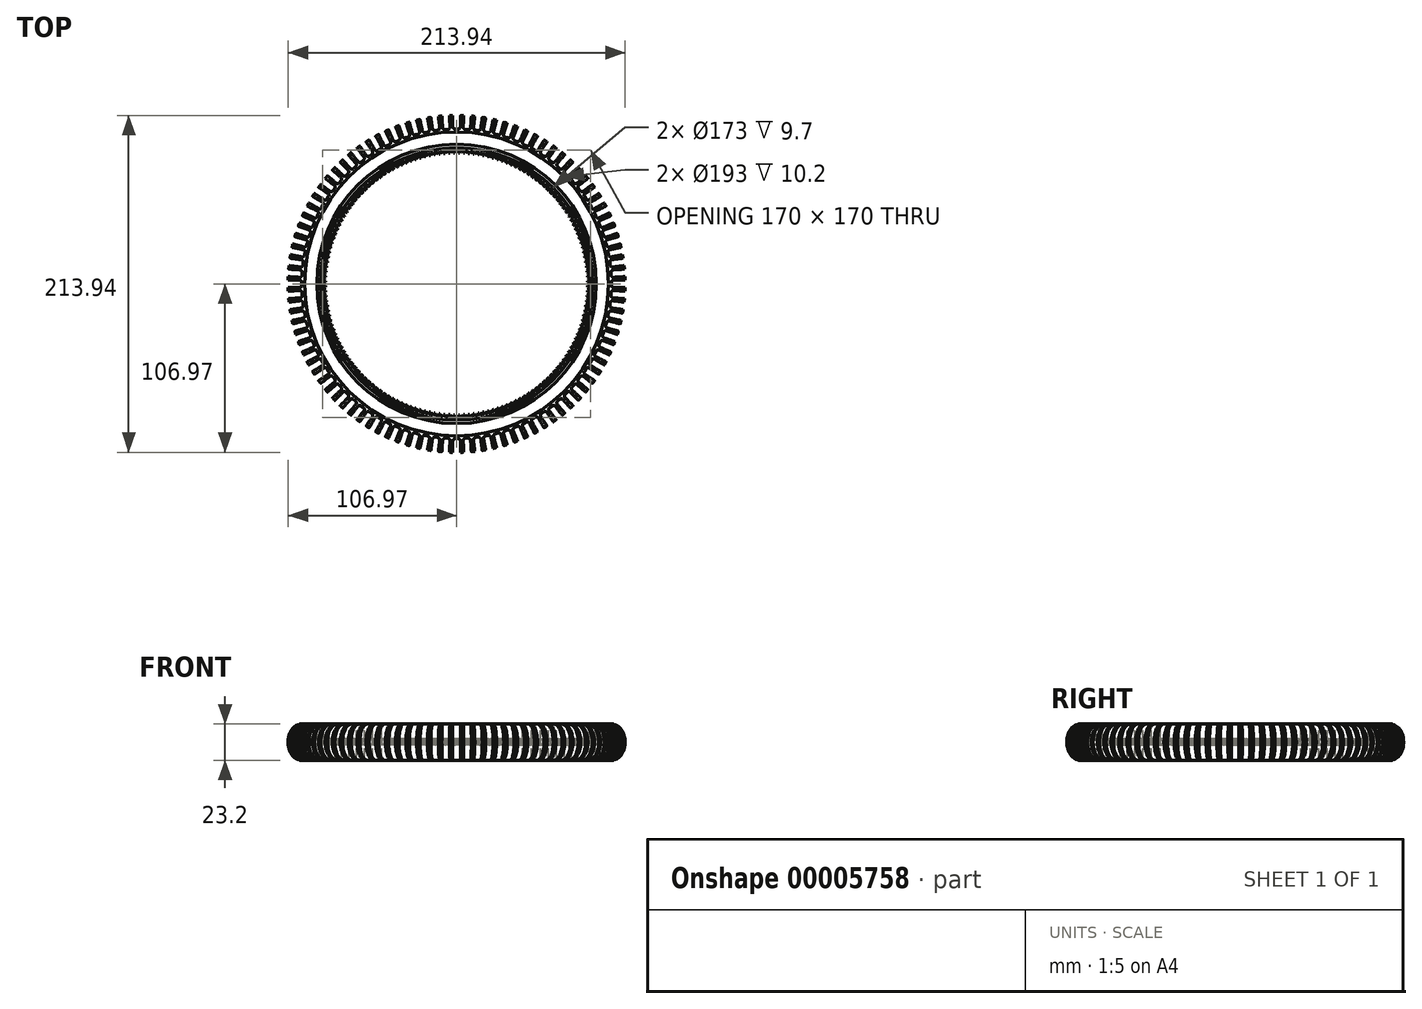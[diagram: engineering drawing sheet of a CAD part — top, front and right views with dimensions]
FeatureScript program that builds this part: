
annotation { "Feature Type Name" : "Feature", "Feature Type Description" : "" }
export const myFeature = defineFeature(function(context is Context, id is Id, definition is map)
    precondition{}
    {
        {
            var Q0;
            Q0=qCreatedBy(makeId("Top.planeOp"),FACE);
            var sketch = newSketch(context, id + "F0", { "sketchPlane" : qUnion([Q0])});
            skCircle(sketch, "E0", {"center": v(0, 0) * mm, "radius": 108 * mm, "construction": true});
            skCircle(sketch, "E1", {"center": v(0, 0) * mm, "radius": 107 * mm});
            skCircle(sketch, "E2", {"center": v(0, 0) * mm, "radius": 86.5 * mm});
            skSolve(sketch);
        }
        {
            var Q0;
            Q0=qCreatedBy(makeId("Top.planeOp"),FACE);
            var sketch = newSketch(context, id + "F1", { "sketchPlane" : qUnion([Q0])});
            skCircle(sketch, "E3", {"center": v(0, 0) * mm, "radius": 88.7 * mm});
            skCircle(sketch, "E4", {"center": v(0, 0) * mm, "radius": 96.5 * mm});
            skCircle(sketch, "E5", {"center": v(0, 0) * mm, "radius": 98.3 * mm});
            skSolve(sketch);
        }
        {
            var Q0;
            Q0=qCreatedBy(makeId("Front.planeOp"),FACE);
            var sketch = newSketch(context, id + "F2", { "sketchPlane" : qUnion([Q0])});
            skLineSegment(sketch, "E6", {"start": v(96.5, 11.6) * mm, "end": v(96.5, 1.4) * mm});
            skLineSegment(sketch, "E7", {"start": v(96.5, 1.4) * mm, "end": v(88.7, 1.4) * mm});
            skLineSegment(sketch, "E8", {"start": v(88.7, 1.4) * mm, "end": v(88.7, 11.6) * mm});
            skLineSegment(sketch, "E9", {"start": v(88.7, 11.6) * mm, "end": v(86.5, 11.6) * mm});
            skLineSegment(sketch, "E10", {"start": v(86.5, 11.6) * mm, "end": v(86.5, -11.6) * mm});
            skLineSegment(sketch, "E11", {"start": v(86.5, 0) * mm, "end": v(0, 0) * mm, "construction": true});
            skLineSegment(sketch, "E12", {"start": v(96.5, 11.6) * mm, "end": v(98.3, 11.6) * mm});
            skLineSegment(sketch, "E13", {"start": v(98.3, 11.6) * mm, "end": v(98.3, 0) * mm, "construction": true});
            skLineSegment(sketch, "E14", {"start": v(88.7, 11.6) * mm, "end": v(96.5, 11.6) * mm, "construction": true});
            skLineSegment(sketch, "E15", {"start": v(88.7, 1.4) * mm, "end": v(88.7, 0) * mm, "construction": true});
            skLineSegment(sketch, "E16", {"start": v(96.5, 1.4) * mm, "end": v(96.5, 0) * mm, "construction": true});
            skLineSegment(sketch, "E17.0.MirrorCS", {"start": v(88.7, -11.6) * mm, "end": v(86.5, -11.6) * mm});
            skLineSegment(sketch, "E18.0.MirrorCS", {"start": v(88.7, -1.4) * mm, "end": v(88.7, -11.6) * mm});
            skLineSegment(sketch, "E19.0.MirrorCS", {"start": v(96.5, -1.4) * mm, "end": v(88.7, -1.4) * mm});
            skLineSegment(sketch, "E20.0.MirrorCS", {"start": v(96.5, -11.6) * mm, "end": v(96.5, -1.4) * mm});
            skLineSegment(sketch, "E21.0.MirrorCS", {"start": v(96.5, -11.6) * mm, "end": v(98.3, -11.6) * mm});
            skEllipticalArc(sketch, "E22", {});
            skLineSegment(sketch, "E23", {"start": v(98.3, 0) * mm, "end": v(107, 0) * mm, "construction": true});
            skLineSegment(sketch, "E24", {"start": v(0, 11.6) * mm, "end": v(0, -11.6) * mm, "construction": true});
            const initialGuessF2  = {"E22": [0.0983, 0, 0, 1, 0.0116, 0.0087, 3.141592653589793, 0]};
            skSetInitialGuess(sketch, initialGuessF2);
            skSolve(sketch);
        }
        {
            var Q0;
            Q0=makeQuery(id+"F2.imprint","IMPRINT",FACE,{"disambiguationData":[TD([[makeQuery(id+"F2.imprint","IMPRINT",EDGE,{"derivedFrom":sQuery(id+"F2.wireOp",EDGE,"E6")}),1.0]])]});
            var Q1;
            Q1=sQuery(id+"F2.wireOp",EDGE,"E24");
            revolve(context, id + "F3", {"entities" : qUnion([Q0]), "axis" : qUnion([Q1]), "revolveType" : RevolveType.FULL});
        }
        {
            var Q0;
            Q0=qCreatedBy(makeId("Top.planeOp"),FACE);
            var sketch = newSketch(context, id + "F4", { "sketchPlane" : qUnion([Q0])});
            skLineSegment(sketch, "E25", {"start": v(0, 0) * mm, "end": v(99.8, 2.4) * mm, "construction": true});
            skLineSegment(sketch, "E26", {"start": v(99.8, -2.4) * mm, "end": v(0, 0) * mm, "construction": true});
            skLineSegment(sketch, "E27", {"start": v(99.8, 2.4) * mm, "end": v(108, 2.4) * mm});
            skLineSegment(sketch, "E28", {"start": v(108, 2.4) * mm, "end": v(108, -2.4) * mm});
            skLineSegment(sketch, "E29", {"start": v(108, -2.4) * mm, "end": v(99.8, -2.4) * mm});
            skLineSegment(sketch, "E30", {"start": v(108, 0) * mm, "end": v(0, 0) * mm, "construction": true});
            skArc(sketch, "E31", {"start": v(99.8, 2.4) * mm, "mid": v(98.74, 1.96) * mm, "end": v(98.3, 0.9) * mm});
            skArc(sketch, "E32", {"start": v(99.8, -2.4) * mm, "mid": v(98.74, -1.96) * mm, "end": v(98.3, -0.9) * mm});
            skLineSegment(sketch, "E33", {"start": v(98.3, 0.9) * mm, "end": v(98.3, -0.9) * mm});
            skSolve(sketch);
        }
        {
            var Q0;
            Q0=makeQuery(id+"F4.imprint","IMPRINT",FACE,{"disambiguationData":[TD([[makeQuery(id+"F4.imprint","IMPRINT",EDGE,{"derivedFrom":sQuery(id+"F4.wireOp",EDGE,"E27")}),-1.0]])]});
            extrude(context, id + "F5", {"entities" : qUnion([Q0]), "operationType" : NewBodyOperationType.REMOVE, "oppositeDirection" : true, "depth" : 25 * mm, "symmetric" : true});
        }
        {
            var Q0;
            Q0=makeQuery(id+"F5.boolean.opBoolean","COPY",FACE,{"derivedFrom":makeQuery(id+"F5.opExtrude","SWEPT_FACE",FACE,{"disambiguationData":[OSD([sQuery(id+"F4.wireOp",EDGE,"E27")])]})});
            var Q1;
            Q1=makeQuery(id+"F5.boolean.opBoolean","COPY",FACE,{"derivedFrom":makeQuery(id+"F5.opExtrude","SWEPT_FACE",FACE,{"disambiguationData":[OSD([sQuery(id+"F4.wireOp",EDGE,"E31")])]})});
            var Q2;
            Q2=makeQuery(id+"F5.boolean.opBoolean","COPY",FACE,{"derivedFrom":makeQuery(id+"F5.opExtrude","SWEPT_FACE",FACE,{"disambiguationData":[OSD([sQuery(id+"F4.wireOp",EDGE,"E33")])]})});
            var Q3;
            Q3=makeQuery(id+"F5.boolean.opBoolean","COPY",FACE,{"derivedFrom":makeQuery(id+"F5.opExtrude","SWEPT_FACE",FACE,{"disambiguationData":[OSD([sQuery(id+"F4.wireOp",EDGE,"E32")])]})});
            var Q4;
            Q4=makeQuery(id+"F5.boolean.opBoolean","COPY",FACE,{"derivedFrom":makeQuery(id+"F5.opExtrude","SWEPT_FACE",FACE,{"disambiguationData":[OSD([sQuery(id+"F4.wireOp",EDGE,"E29")])]})});
            var Q5;
            Q5=sQuery(id+"F2.wireOp",EDGE,"E24");
            circularPattern(context, id + "F6", {"faces" : qUnion([Q0, Q1, Q2, Q3, Q4]), "axis" : qUnion([Q5]), "angle" : 360 * degree, "instanceCount" : 96, "equalSpace" : true, "patternType" : PatternType.FACE});
        }
        {
            var Q0;
            Q0=qCreatedBy(makeId("Top.planeOp"),FACE);
            var sketch = newSketch(context, id + "F7", { "sketchPlane" : qUnion([Q0])});
            skLineSegment(sketch, "E34", {"start": v(0, 0) * mm, "end": v(83.19, 1.56) * mm, "construction": true});
            skLineSegment(sketch, "E35", {"start": v(0, 0) * mm, "end": v(83.19, -1.56) * mm, "construction": true});
            skArc(sketch, "E36.0", {"start": v(86.48, -1.62) * mm, "mid": v(86.5, 0) * mm, "end": v(86.48, 1.62) * mm, "construction": true});
            skLineSegment(sketch, "E37", {"start": v(83.19, 1.56) * mm, "end": v(86.48, 1.62) * mm, "construction": true});
            skLineSegment(sketch, "E38", {"start": v(83.19, -1.56) * mm, "end": v(86.48, -1.62) * mm, "construction": true});
            skLineSegment(sketch, "E39", {"start": v(86.5, 0) * mm, "end": v(0, 0) * mm, "construction": true});
            skLineSegment(sketch, "E40", {"start": v(83.2, 1.2) * mm, "end": v(85, 0.53) * mm});
            skLineSegment(sketch, "E41", {"start": v(83.2, -1.2) * mm, "end": v(85, -0.53) * mm});
            skPoint(sketch, "E42", {"position": v(85, 0) * mm});
            skCircle(sketch, "E43", {"center": v(0, 0) * mm, "radius": 84 * mm, "construction": true});
            skArc(sketch, "E44", {"start": v(85, -0.53) * mm, "mid": v(85, 0) * mm, "end": v(85, 0.53) * mm});
            skArc(sketch, "E45", {"start": v(83.19, -1.56) * mm, "mid": v(83.19, -1.37) * mm, "end": v(83.2, -1.2) * mm, "construction": true});
            skArc(sketch, "E46", {"start": v(83.2, 1.2) * mm, "mid": v(83.19, 1.37) * mm, "end": v(83.19, 1.56) * mm, "construction": true});
            skArc(sketch, "E47", {"start": v(83.2, -1.2) * mm, "mid": v(83.2, 0) * mm, "end": v(83.2, 1.2) * mm});
            skPoint(sketch, "E48", {"position": v(84, 0.9) * mm});
            skPoint(sketch, "E49", {"position": v(84, -0.9) * mm});
            skSolve(sketch);
        }
        {
            var Q0;
            Q0=qCreatedBy(makeId("Top.planeOp"),FACE);
            var sketch = newSketch(context, id + "F8", { "sketchPlane" : qUnion([Q0])});
            skCircle(sketch, "E50", {"center": v(0, 0) * mm, "radius": 83.2 * mm});
            skCircle(sketch, "E51", {"center": v(0, 0) * mm, "radius": 86.5 * mm});
            skSolve(sketch);
        }
        {
            var Q0;
            Q0 = qSketchRegion(id + "F8", true);
            extrude(context, id + "F9", {"entities" : qUnion([Q0]), "operationType" : NewBodyOperationType.ADD, "depth" : 3.8 * mm, "symmetric" : true});
        }
        {
            var Q0;
            Q0 = qSketchRegion(id + "F7", true);
            extrude(context, id + "F10", {"entities" : qUnion([Q0]), "operationType" : NewBodyOperationType.REMOVE, "oppositeDirection" : true, "depth" : 25 * mm, "symmetric" : true});
        }
        {
            var Q0;
            Q0=makeQuery(id+"F10.boolean.opBoolean","COPY",FACE,{"derivedFrom":makeQuery(id+"F10.opExtrude","SWEPT_FACE",FACE,{"disambiguationData":[OSD([sQuery(id+"F7.wireOp",EDGE,"E40")])]})});
            var Q1;
            Q1=makeQuery(id+"F10.boolean.opBoolean","COPY",FACE,{"derivedFrom":makeQuery(id+"F10.opExtrude","SWEPT_FACE",FACE,{"disambiguationData":[OSD([sQuery(id+"F7.wireOp",EDGE,"E44")])]})});
            var Q2;
            Q2=makeQuery(id+"F10.boolean.opBoolean","COPY",FACE,{"derivedFrom":makeQuery(id+"F10.opExtrude","SWEPT_FACE",FACE,{"disambiguationData":[OSD([sQuery(id+"F7.wireOp",EDGE,"E41")])]})});
            var Q3;
            Q3=sQuery(id+"F2.wireOp",EDGE,"E24");
            circularPattern(context, id + "F11", {"faces" : qUnion([Q0, Q1, Q2]), "axis" : qUnion([Q3]), "angle" : 360 * degree, "instanceCount" : 168, "equalSpace" : true, "patternType" : PatternType.FACE});
        }
    });
